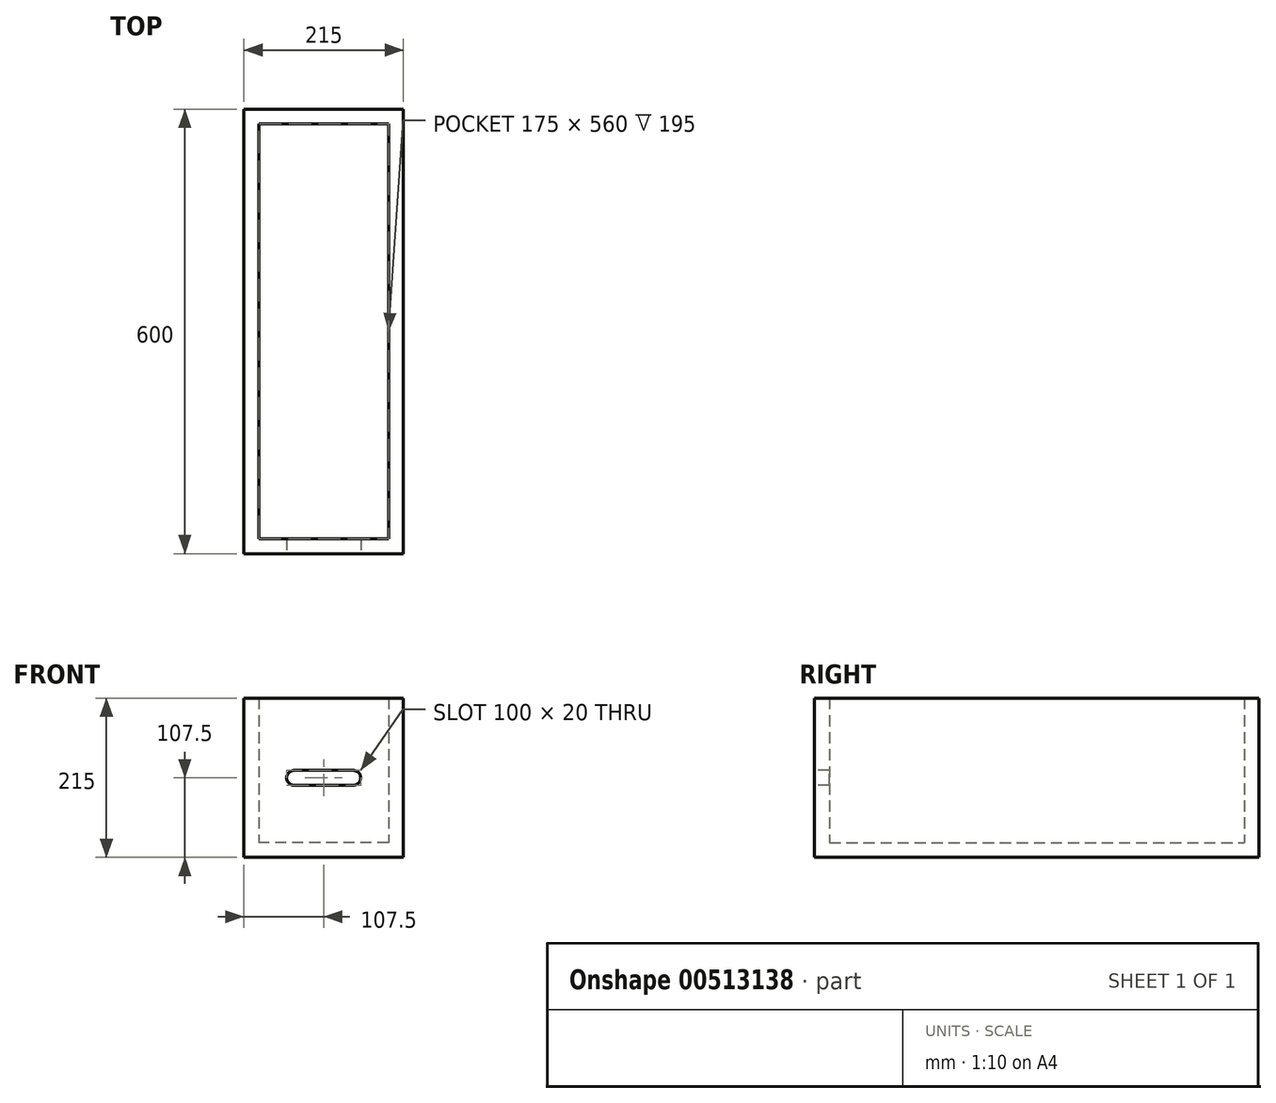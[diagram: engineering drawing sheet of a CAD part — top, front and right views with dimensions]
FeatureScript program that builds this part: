
annotation { "Feature Type Name" : "Feature", "Feature Type Description" : "" }
export const myFeature = defineFeature(function(context is Context, id is Id, definition is map)
    precondition{}
    {
        {
            var Q0;
            Q0=qCreatedBy(makeId("Front.planeOp"),FACE);
            var sketch = newSketch(context, id + "F0", { "sketchPlane" : qUnion([Q0])});
            skLineSegment(sketch, "E0.bottom", {"start": v(107.5, 107.5) * mm, "end": v(-107.5, 107.5) * mm});
            skLineSegment(sketch, "E0.top", {"start": v(107.5, -107.5) * mm, "end": v(-107.5, -107.5) * mm});
            skLineSegment(sketch, "E0.left", {"start": v(107.5, 107.5) * mm, "end": v(107.5, -107.5) * mm});
            skLineSegment(sketch, "E0.right", {"start": v(-107.5, 107.5) * mm, "end": v(-107.5, -107.5) * mm});
            skPoint(sketch, "E0.middle", {"position": v(0, 0) * mm});
            skSolve(sketch);
        }
        {
            var Q0;
            Q0 = qSketchRegion(id + "F0", true);
            extrude(context, id + "F1", {"entities" : qUnion([Q0]), "depth" : 600 * mm, "offsetDistance" : 25 * mm});
        }
        {
            var Q0;
            Q0=makeQuery(id+"F1.opExtrude","SWEPT_FACE",FACE,{"disambiguationData":[OSD([sQuery(id+"F0.wireOp",EDGE,"E0.bottom")])]});
            shell(context, id + "F2", {"entities" : qUnion([Q0]), "thickness" : 20 * mm});
        }
        {
            var Q0;
            Q0=makeQuery(id+"F1.opExtrude","CAP_FACE",FACE,{"disambiguationData":[OSD([sQuery(id+"F0.wireOp",EDGE,"E0.bottom"),sQuery(id+"F0.wireOp",EDGE,"E0.top"),sQuery(id+"F0.wireOp",EDGE,"E0.left"),sQuery(id+"F0.wireOp",EDGE,"E0.right")])],"isStart":false});
            var sketch = newSketch(context, id + "F3", { "sketchPlane" : qUnion([Q0])});
            skLineSegment(sketch, "E1.bottom", {"start": v(40, -10) * mm, "end": v(-40, -10) * mm});
            skLineSegment(sketch, "E1.top", {"start": v(40, 10) * mm, "end": v(-40, 10) * mm});
            skPoint(sketch, "E1.middle", {"position": v(0, 0) * mm});
            skArc(sketch, "E2", {"start": v(-40, 10) * mm, "mid": v(-50, 0) * mm, "end": v(-40, -10) * mm});
            skPoint(sketch, "E2.centerSnap0", {"position": v(-50, 0) * mm});
            skArc(sketch, "E3", {"start": v(40, -10) * mm, "mid": v(50, 0) * mm, "end": v(40, 10) * mm});
            skPoint(sketch, "E3.centerSnap0", {"position": v(50, 0) * mm});
            skPoint(sketch, "E4.orphan", {"position": v(-50, -10) * mm});
            skPoint(sketch, "E5.orphan", {"position": v(50, 10) * mm});
            skPoint(sketch, "E6.orphan", {"position": v(50, -10) * mm});
            skPoint(sketch, "E7.orphan", {"position": v(-50, 10) * mm});
            skSolve(sketch);
        }
        {
            var Q0;
            Q0 = qSketchRegion(id + "F3", true);
            extrude(context, id + "F4", {"entities" : qUnion([Q0]), "operationType" : NewBodyOperationType.REMOVE, "endBound" : BoundingType.UP_TO_NEXT, "oppositeDirection" : true, "depth" : 25 * mm, "offsetDistance" : 25 * mm});
        }
    });
